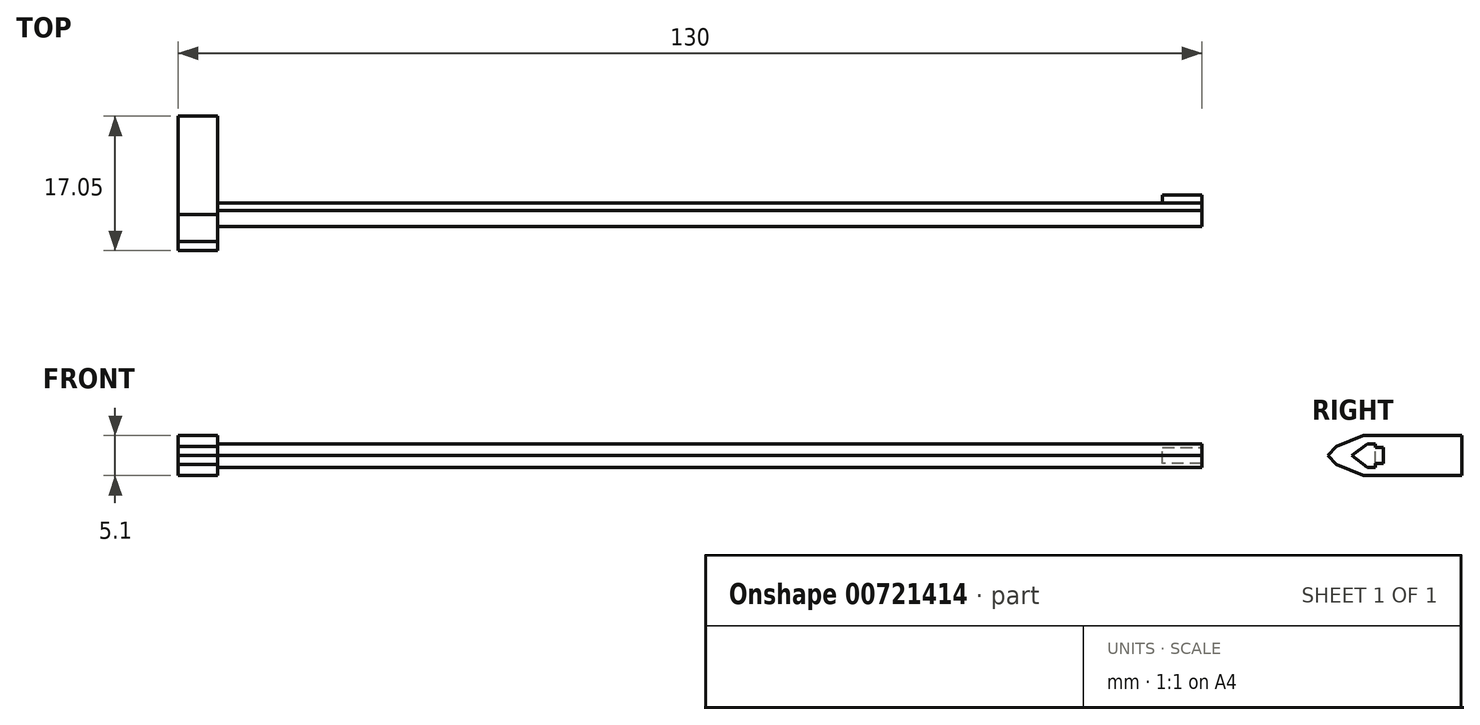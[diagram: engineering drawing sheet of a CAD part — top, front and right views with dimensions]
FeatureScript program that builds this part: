
annotation { "Feature Type Name" : "Feature", "Feature Type Description" : "" }
export const myFeature = defineFeature(function(context is Context, id is Id, definition is map)
    precondition{}
    {
        {
            var Q0;
            Q0=qCreatedBy(makeId("Right.planeOp"),FACE);
            var sketch = newSketch(context, id + "F0", { "sketchPlane" : qUnion([Q0])});
            skLineSegment(sketch, "E0", {"start": v(-9.1, -8.66) * mm, "end": v(-6.6, -8.66) * mm});
            skLineSegment(sketch, "E1", {"start": v(-6.6, -8.66) * mm, "end": v(-6.6, -3.56) * mm});
            skLineSegment(sketch, "E2", {"start": v(-6.6, -3.56) * mm, "end": v(-9.1, -3.56) * mm});
            skLineSegment(sketch, "E3", {"start": v(-9.1, -8.66) * mm, "end": v(-12.52, -7.24) * mm});
            skLineSegment(sketch, "E4", {"start": v(-12.52, -7.24) * mm, "end": v(-13.65, -6.1) * mm});
            skLineSegment(sketch, "E5", {"start": v(-13.65, -6.1) * mm, "end": v(-12.52, -4.97) * mm});
            skLineSegment(sketch, "E6", {"start": v(-12.52, -4.97) * mm, "end": v(-9.1, -3.56) * mm});
            skLineSegment(sketch, "E7", {"start": v(-7.6, -7.6) * mm, "end": v(-7.6, -4.6) * mm});
            skLineSegment(sketch, "E8", {"start": v(-7.6, -4.6) * mm, "end": v(-8.6, -4.6) * mm});
            skLineSegment(sketch, "E9", {"start": v(-8.6, -4.6) * mm, "end": v(-10.6, -6.1) * mm});
            skLineSegment(sketch, "E10", {"start": v(-10.6, -6.1) * mm, "end": v(-8.6, -7.6) * mm});
            skLineSegment(sketch, "E11", {"start": v(-8.6, -7.6) * mm, "end": v(-7.6, -7.6) * mm});
            skSolve(sketch);
        }
        {
            var Q0;
            Q0=makeQuery(id+"F0.imprint","IMPRINT",FACE,{"disambiguationData":[TD([[makeQuery(id+"F0.imprint","IMPRINT",EDGE,{"derivedFrom":sQuery(id+"F0.wireOp",EDGE,"E7")}),1.0]])]});
            extrude(context, id + "F1", {"entities" : qUnion([Q0]), "depth" : 125 * mm, "offsetDistance" : 25 * mm});
        }
        {
            var Q0;
            Q0=makeQuery(id+"F0.imprint","IMPRINT",FACE,{"disambiguationData":[TD([[makeQuery(id+"F0.imprint","IMPRINT",EDGE,{"derivedFrom":sQuery(id+"F0.wireOp",EDGE,"E7")}),1.0]])]});
            var Q1;
            Q1=makeQuery(id+"F0.imprint","IMPRINT",FACE,{"disambiguationData":[TD([[makeQuery(id+"F0.imprint","IMPRINT",EDGE,{"derivedFrom":sQuery(id+"F0.wireOp",EDGE,"E0")}),1.0]])]});
            extrude(context, id + "F2", {"entities" : qUnion([Q0, Q1]), "operationType" : NewBodyOperationType.ADD, "oppositeDirection" : true, "depth" : 5 * mm, "offsetDistance" : 25 * mm});
        }
        {
            var Q0;
            Q0=makeQuery(id+"F1.opExtrude","SWEPT_FACE",FACE,{"disambiguationData":[OSD([sQuery(id+"F0.wireOp",EDGE,"E7")])]});
            var sketch = newSketch(context, id + "F3", { "sketchPlane" : qUnion([Q0])});
            skLineSegment(sketch, "E12", {"start": v(-120, -7.1) * mm, "end": v(-120, -5.1) * mm});
            skLineSegment(sketch, "E13", {"start": v(-120, -7.1) * mm, "end": v(-120, -6.1) * mm});
            skPoint(sketch, "E14.orphan", {"position": v(-120, -4.6) * mm});
            skLineSegment(sketch, "E15", {"start": v(-120, -5.1) * mm, "end": v(-125, -5.1) * mm});
            skLineSegment(sketch, "E16", {"start": v(-125, -5.1) * mm, "end": v(-125, -7.1) * mm});
            skPoint(sketch, "E17.start.orphan", {"position": v(-120, -6.1) * mm});
            skLineSegment(sketch, "E18", {"start": v(-125, -7.1) * mm, "end": v(-120, -7.1) * mm});
            skSolve(sketch);
        }
        {
            var Q0;
            Q0 = qSketchRegion(id + "F3", true);
            extrude(context, id + "F4", {"entities" : qUnion([Q0]), "operationType" : NewBodyOperationType.ADD, "depth" : 1 * mm, "offsetDistance" : 25 * mm});
        }
        {
            var Q0;
            Q0=makeQuery(id+"F2.opExtrude","SWEPT_FACE",FACE,{"disambiguationData":[OSD([sQuery(id+"F0.wireOp",EDGE,"E1")])]});
            extrude(context, id + "F5", {"entities" : qUnion([Q0]), "operationType" : NewBodyOperationType.ADD, "depth" : 10 * mm, "offsetDistance" : 25 * mm});
        }
    });
